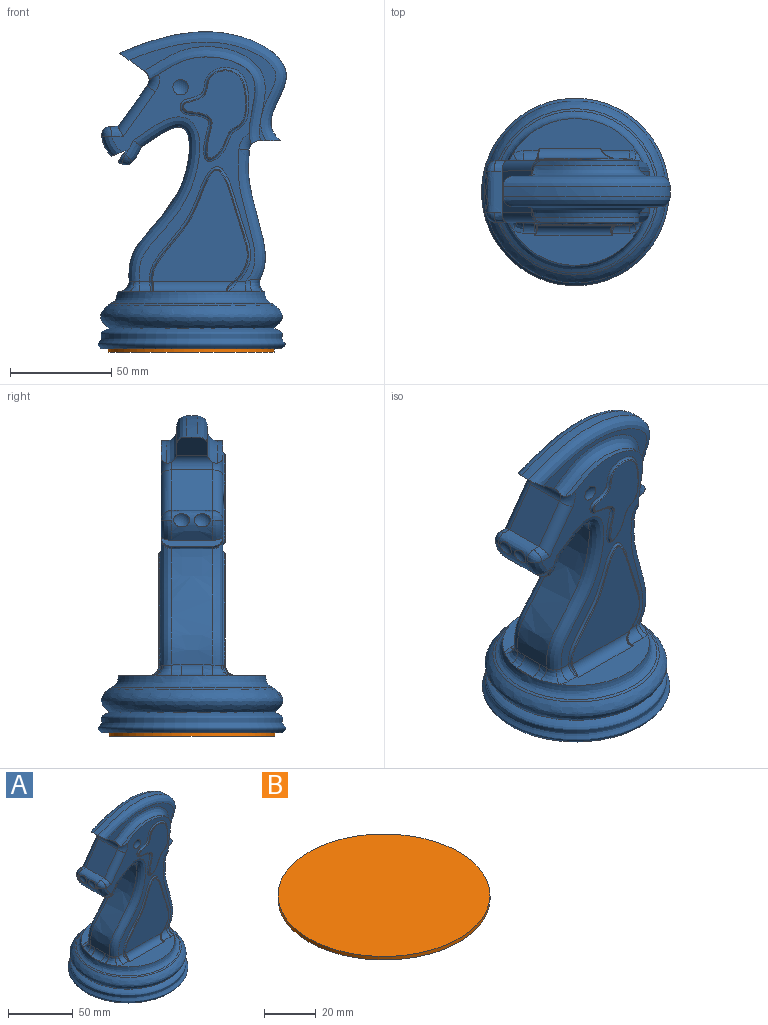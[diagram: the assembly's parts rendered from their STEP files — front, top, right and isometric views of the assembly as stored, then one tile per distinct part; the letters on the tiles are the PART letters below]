
ASSEMBLY  parts=2 mates=1
PART A: 100 faces, bbox 191.1x183.7x247.5 mm
  f0: extruded ~2.29x1.9mm, area 0.9mm2, adj f70,f94,f99
  f1: plane 61.07x17.38mm, normal (0,0,1), area 629.6mm2, adj f9,f61,f69,f70,f76,f77,f95,f99
  f2: plane 10.79x0.4mm, normal (0,0,1), area 2.9mm2, adj f9,f66
  f3: plane 203.07x162.64mm, normal (0,1,0), area 1686.8mm2, adj f7,f15,f16,f25,f34,f35,f41,f43
  f4: plane 111.88x71.45mm, normal (0,-1,0), area 1699.4mm2, adj f13,f15,f16,f24,f32,f33,f36,f38
  f5: plane 61.03x17.33mm, normal (0,0,1), area 620.1mm2, adj f9,f60,f62,f63,f71,f72,f79,f83
  f6: extruded ~20.32x14.77mm, area 367.2mm2, adj f14,f15,f36,f37,f38,f41,f42,f43
  f7: extruded ~51.52x42.56mm, area 214.4mm2, adj f3,f26,f35,f45
  f8: plane 89.29x89.29mm, normal (0,0,-1), area 6261.6mm2, adj f11
  f9: revolved ~79.74x79.74mm, area 1752.2mm2, adj f1,f2,f5,f64,f65,f67,f68,f73
  f10: revolved ~89.65x89.65mm, area 3942.7mm2, adj f11,f78
  f11: revolved ~92.49x92.49mm, area 3866.1mm2, adj f8,f10
  f12: extruded ~63.62x20.32mm, area 1320.9mm2, adj f29,f32,f34,f74
  f13: extruded ~51.52x42.56mm, area 214.4mm2, adj f4,f27,f33,f40
  f14: plane 20.32x20.01mm, normal (-0.81,0,0.58), area 500.5mm2, adj f6,f28,f39,f44
  f15: plane 31.32x7.6mm, normal (0.38,0,-0.92), area 211.2mm2, adj f3,f4,f6,f16,f36,f41
  f16: plane 30.66x5.86mm, normal (-0.86,0,0.52), area 191.3mm2, adj f3,f4,f15,f17,f46,f49
  f17: extruded ~20.32x11.51mm, area 331.2mm2, adj f16,f18,f46,f47,f48,f49,f50,f51
  f18: extruded ~75.82x29.81mm, area 2196.3mm2, adj f17,f24,f25,f65,f66,f67
  f19: plane 16.58x13.92mm, normal (-0.58,0,-0.81), area 224.2mm2, adj f21,f22,f23,f26,f27,f28,f30,f31
  f20: plane 16.53x11.75mm, normal (0,0,-1), area 143.4mm2, adj f21,f22,f23,f26,f27,f29,f30,f31
  f21: extruded ~82.34x53.67mm, area 651.3mm2, adj f19,f20,f30,f31
  f22: plane 72.49x48.61mm, normal (0,-1,0), area 354mm2, adj f19,f20,f27,f31
  f23: plane 72.5x48.62mm, normal (0,1,0), area 354.1mm2, adj f19,f20,f26,f30
  f24: bspline ~83.58x40.93mm, area 900.9mm2, adj f4,f18,f48,f63,f64
  f25: bspline ~83.58x40.93mm, area 900.9mm2, adj f3,f18,f51,f68,f69
  f26: bspline ~89.56x49.15mm, area 742.3mm2, adj f7,f19,f20,f23,f28,f29,f35,f45
  f27: bspline ~89.56x49.15mm, area 742.3mm2, adj f13,f19,f20,f22,f28,f29,f33,f40
  f28: cylinder r=5.08mm len=20.32mm, axis (0,-1,0), area 152.2mm2, adj f14,f19,f26,f27,f40,f45
  f29: cylinder r=5.08mm len=20.32mm, axis (0,1,0), area 143.8mm2, adj f12,f20,f26,f27,f33,f35
  f30: bspline ~84.91x57.94mm, area 974.8mm2, adj f19,f20,f21,f23
  f31: bspline ~84.91x57.94mm, area 974.8mm2, adj f19,f20,f21,f22
  f32: bspline ~73.05x13.45mm, area 526.7mm2, adj f4,f12,f33,f72,f73
  f33: torus R=10.16mm, axis (0,-1,0), area 42.4mm2, adj f4,f13,f27,f29,f32
  f34: bspline ~73.05x13.45mm, area 526.7mm2, adj f3,f12,f35,f75,f76
  f35: torus R=10.16mm, axis (0,-1,0), area 42.4mm2, adj f3,f7,f26,f29,f34
  f36: bspline ~12.23x10.09mm, area 83.8mm2, adj f4,f6,f15,f37
  f37: bspline ~5.12x5.08mm, area 35.6mm2, adj f6,f36,f38
  f38: bspline ~9.57x5.26mm, area 36.8mm2, adj f4,f6,f37,f39
  f39: cylinder r=5.08mm len=25.16mm, axis (0.58,0,0.81), area 207.3mm2, adj f4,f14,f38,f40
  f40: torus R=10.16mm, axis (0,-1,0), area 43.2mm2, adj f4,f13,f27,f28,f39
  f41: bspline ~12.23x10.09mm, area 83.8mm2, adj f3,f6,f15,f42
  f42: bspline ~5.12x5.08mm, area 22.9mm2, adj f6,f41,f43
  f43: bspline ~9.57x5.26mm, area 36.8mm2, adj f3,f6,f42,f44
  f44: cylinder r=5.08mm len=25.16mm, axis (-0.58,0,-0.81), area 207.3mm2, adj f3,f14,f43,f45
  f45: torus R=10.16mm, axis (0,-1,0), area 43.2mm2, adj f3,f7,f26,f28,f44
  f46: bspline ~6.41x5.43mm, area 12.6mm2, adj f4,f16,f17,f47
  f47: bspline ~5.36x5.2mm, area 18.8mm2, adj f17,f46,f48
  f48: bspline ~25.64x16.04mm, area 67.9mm2, adj f4,f17,f24,f47
  f49: bspline ~6.41x5.43mm, area 12.6mm2, adj f3,f16,f17,f50
  f50: bspline ~5.36x5.2mm, area 18.8mm2, adj f17,f49,f51
  f51: bspline ~25.71x16.06mm, area 67.9mm2, adj f3,f17,f25,f50
  f52: sphere r=6.35mm, area 50.7mm2, adj f4
  f53: sphere r=6.35mm, area 50.7mm2, adj f3
  f54: sphere r=5.08mm, area 48.3mm2, adj f6
  f55: sphere r=5.08mm, area 48.3mm2, adj f6
  f56: plane 54.88x46.53mm, normal (0,-1,0), area 1466.9mm2, adj f60,f86,f87,f88
  f57: plane 42.97x30.56mm, normal (0,-1,0), area 648.9mm2, adj f92
  f58: extruded ~2.13x1.48mm, area 0.5mm2, adj f77,f94,f95
  f59: plane 54.89x46.54mm, normal (0,1,0), area 1474.6mm2, adj f61,f97
  f60: cylinder r=5.08mm len=40.65mm, axis (-1,0,0), area 298.1mm2, adj f5,f56,f84,f85,f89,f90
  f61: cylinder r=5.08mm len=39.43mm, axis (-1,0,0), area 274.1mm2, adj f1,f59,f95,f96,f98,f99
  f62: cylinder r=5.08mm len=5.58mm, axis (-1,0,0), area 42.1mm2, adj f4,f5,f63,f82
  f63: bspline ~7.06x6.16mm, area 30.5mm2, adj f5,f24,f62,f64
  f64: bspline ~10.47x7.15mm, area 47.6mm2, adj f9,f24,f63,f65
  f65: bspline ~5.35x5.08mm, area 35.8mm2, adj f9,f18,f64,f66
  f66: cylinder r=5.08mm len=10.79mm, axis (0,1,0), area 89mm2, adj f2,f18,f65,f67
  f67: bspline ~5.35x5.08mm, area 35.9mm2, adj f9,f18,f66,f68
  f68: bspline ~10.22x7mm, area 47.6mm2, adj f9,f25,f67,f69
  f69: bspline ~6.8x6.07mm, area 30.5mm2, adj f1,f25,f68,f70
  f70: cylinder r=5.08mm len=7.39mm, axis (1,0,0), area 52mm2, adj f0,f1,f3,f69,f94,f99
  f71: cylinder r=5.08mm len=8.53mm, axis (-1,0,0), area 49mm2, adj f4,f5,f72,f80
  f72: bspline ~6.27x5.99mm, area 21.9mm2, adj f5,f32,f71,f73
  f73: bspline ~12.04x6.93mm, area 56.5mm2, adj f9,f32,f72,f74
  f74: bspline ~20.32x6.75mm, area 144.2mm2, adj f9,f12,f73,f75
  f75: bspline ~12.29x6.75mm, area 56.5mm2, adj f9,f34,f74,f76
  f76: bspline ~6.47x6.45mm, area 21.9mm2, adj f1,f34,f75,f77
  f77: cylinder r=5.08mm len=13.65mm, axis (1,0,0), area 77mm2, adj f1,f3,f58,f76,f94,f95
  f78: torus R=37.83mm, axis (0,0,-1), area 336.4mm2, adj f9,f10
  f79: cylinder r=1.27mm len=1.27mm, axis (0,1,0), area 0.3mm2, adj f5,f80,f84
  f80: bspline ~8.98x6.9mm, area 14.1mm2, adj f71,f79,f81,f85,f86
  f81: bspline ~58.67x49.95mm, area 206.8mm2, adj f4,f80,f82,f87
  f82: bspline ~6.27x5.45mm, area 10mm2, adj f62,f81,f83,f88,f89
  f83: cylinder r=1.27mm len=1.27mm, axis (0,1,0), area 0.3mm2, adj f5,f82,f90
  f84: bspline ~2.29x1.23mm, area 0.1mm2, adj f60,f79,f85
  f85: bspline ~5.77x4.56mm, area 3.7mm2, adj f60,f80,f84,f86
  f86: bspline ~2.43x2.34mm, area 1.1mm2, adj f56,f80,f85,f87
  f87: bspline ~57.68x47.51mm, area 81.1mm2, adj f56,f81,f86,f88
  f88: bspline ~0.52x0.51mm, area 0.1mm2, adj f56,f82,f87,f89
  f89: bspline ~5.53x4.33mm, area 3.5mm2, adj f60,f82,f88,f90
  f90: bspline ~2.29x1.23mm, area 0.1mm2, adj f60,f83,f89
  f91: bspline ~46.12x33.93mm, area 210.2mm2, adj f4,f92
  f92: bspline ~43.94x31.53mm, area 80mm2, adj f57,f91
  f93: bspline ~36.1x24.09mm, area 0mm2, adj f3
  f94: bspline ~61.72x49.95mm, area 215.4mm2, adj f0,f3,f58,f70,f77,f96,f97,f98
  f95: bspline ~5.51x5.41mm, area 6mm2, adj f1,f58,f61,f77,f96
  f96: bspline ~4.82x3.76mm, area 3.1mm2, adj f61,f94,f95,f97
  f97: bspline ~57.82x47.52mm, area 82.1mm2, adj f59,f94,f96,f98
  f98: bspline ~3.81x1mm, area 1.7mm2, adj f61,f94,f97,f99
  f99: bspline ~6.03x4.65mm, area 3.9mm2, adj f0,f1,f61,f70,f98
PART B: 3 faces, bbox 81.9x81.9x1.7 mm
  f0: plane 81.87x81.87mm, normal (0,0,1), area 5264.1mm2, adj f1
  f1: cylinder r=40.93mm len=81.87mm, axis (0,0,-1), area 427.5mm2, adj f0,f2
  f2: plane 81.87x81.87mm, normal (0,0,-1), area 5264.1mm2, adj f1
PLACE A t=(1.45,0.51,-0.22)mm
PLACE B t=(1.45,0.51,-0.22)mm
MATE fastened B.f1 <-> A.f78  axis (0,0,1) through (357.08,-253.49,26.78)mm
